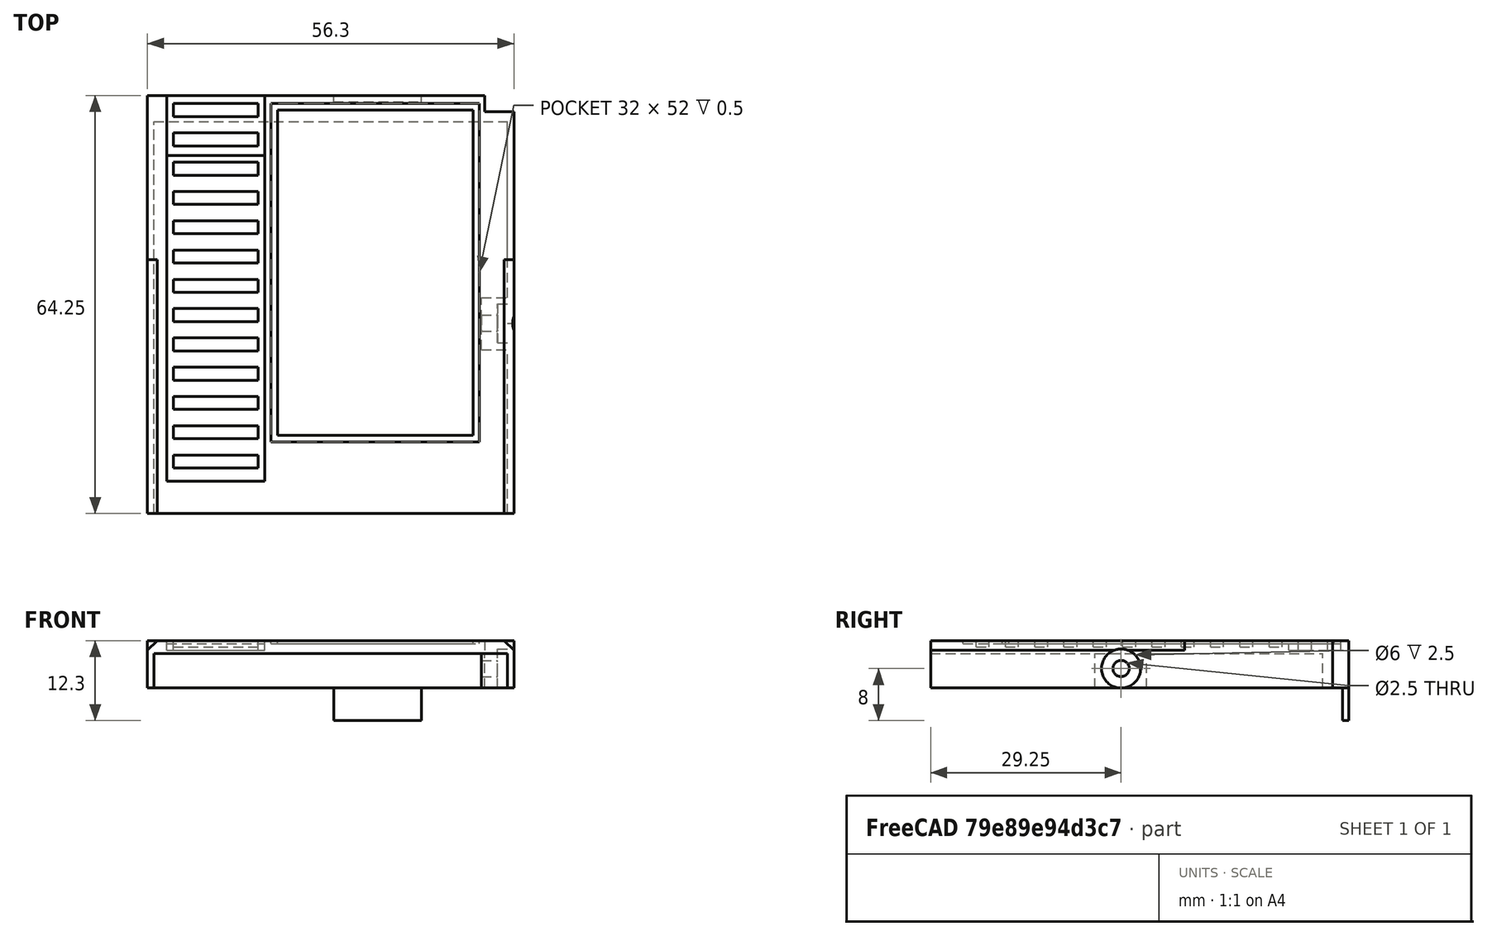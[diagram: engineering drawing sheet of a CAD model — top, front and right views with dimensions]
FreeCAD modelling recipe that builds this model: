
FCSTD DOCUMENT  (FreeCAD 0.18R16131 (Git))
Label: GBC_cart_cover
License: All rights reserved
LicenseURL: http://en.wikipedia.org/wiki/All_rights_reserved
objects: Part::Box×26, Part::Cut×7, Part::MultiFuse×5, Part::Cylinder×2, Part::Chamfer×1
note: 41 computed .brp shape members not serialized (recipe doc carries the construction recipe); baked Part::Feature solids carry a one-line shape summary decoded from their .brp

FEATURE [Part::Box] Box  label="Cube(outer_base)"
  AttacherType = Attacher::AttachEngine3D
  Height = 5.3
  Length = 56.3
  Width = 64.25
FEATURE [Part::Box] Box001  label="Cube(corner_inner)"
  AttacherType = Attacher::AttachEngine3D
  Height = 5.3
  Length = 4.5
  Placement = pos=(51.8,61.75,0) rot=(0,0,1;0rad)
  Width = 2.5
FEATURE [Part::Box] Box007  label="Cube(top_cover_top_half)"
  AttacherType = Attacher::AttachEngine3D
  Height = 2
  Length = 56.3
  Placement = pos=(0,39,5.3) rot=(0,0,1;0rad)
  Width = 25.25
FEATURE [Part::Box] Box008  label="Cube001(top_cover_bottom_half)"
  AttacherType = Attacher::AttachEngine3D
  Height = 2
  Length = 56.3
  Placement = pos=(0,0,5.3) rot=(0,0,1;0rad)
  Width = 39
FEATURE [Part::Box] Box010  label="Cube(top_corner_cut)"
  AttacherType = Attacher::AttachEngine3D
  Height = 10
  Length = 10
  Placement = pos=(51.8,61.75,0) rot=(0,0,1;0rad)
  Width = 10
FEATURE [Part::Cut] Cut006
  Base = -> Box007
  Tool = -> Box010
FEATURE [Part::Box] Box017  label="Cube(game_lable_inner)"
  AttacherType = Attacher::AttachEngine3D
  Height = 0.5
  Length = 30
  Placement = pos=(20,12,6.8) rot=(0,0,1;0rad)
  Width = 50
FEATURE [Part::Box] Box018  label="Cube(cube_strips)"
  AttacherType = Attacher::AttachEngine3D
  Height = 0.5
  Length = 15
  Placement = pos=(3,5,6.8) rot=(0,0,1;0rad)
  Width = 53
FEATURE [Part::Box] Box019  label="Cube(cube_strip_top)"
  AttacherType = Attacher::AttachEngine3D
  Height = 1.5
  Length = 15
  Placement = pos=(3,55,5.8) rot=(0,0,1;0rad)
  Width = 9.25
FEATURE [Part::Box] Box020  label="Cube(ladders)"
  AttacherType = Attacher::AttachEngine3D
  Height = 1
  Length = 13
  Placement = pos=(4,7,6.3) rot=(0,0,1;0rad)
  Width = 2
FEATURE [Part::Box] Box021  label="Cube(ladders)001"
  AttacherType = Attacher::AttachEngine3D
  Height = 1
  Length = 13
  Placement = pos=(4,11.5,6.3) rot=(0,0,1;0rad)
  Width = 2
FEATURE [Part::Box] Box022  label="Cube(ladders)002"
  AttacherType = Attacher::AttachEngine3D
  Height = 1
  Length = 13
  Placement = pos=(4,16,6.3) rot=(0,0,1;0rad)
  Width = 2
FEATURE [Part::Box] Box023  label="Cube(ladders)003"
  AttacherType = Attacher::AttachEngine3D
  Height = 1
  Length = 13
  Placement = pos=(4,20.5,6.3) rot=(0,0,1;0rad)
  Width = 2
FEATURE [Part::Box] Box024  label="Cube(ladders)004"
  AttacherType = Attacher::AttachEngine3D
  Height = 1
  Length = 13
  Placement = pos=(4,25,6.3) rot=(0,0,1;0rad)
  Width = 2
FEATURE [Part::Box] Box025  label="Cube(ladders)005"
  AttacherType = Attacher::AttachEngine3D
  Height = 1
  Length = 13
  Placement = pos=(4,29.5,6.3) rot=(0,0,1;0rad)
  Width = 2
FEATURE [Part::Box] Box029  label="Cube(cube_strip_top_outer)"
  AttacherType = Attacher::AttachEngine3D
  Height = 1.5
  Length = 17
  Placement = pos=(2,55,5.8) rot=(0,0,1;0rad)
  Width = 9.25
FEATURE [Part::MultiFuse] Fusion003
  Shapes = -> [Cut006,Box029]
FEATURE [Part::Cut] Cut008
  Base = -> Fusion003
  Tool = -> Box019
FEATURE [Part::Box] Box030  label="Cube(ladders)009"
  AttacherType = Attacher::AttachEngine3D
  Height = 1
  Length = 13
  Placement = pos=(4,34,6.3) rot=(0,0,1;0rad)
  Width = 2
FEATURE [Part::Box] Box031  label="Cube(ladders)010"
  AttacherType = Attacher::AttachEngine3D
  Height = 1
  Length = 13
  Placement = pos=(4,38.5,6.3) rot=(0,0,1;0rad)
  Width = 2
FEATURE [Part::Box] Box032  label="Cube(ladders)011"
  AttacherType = Attacher::AttachEngine3D
  Height = 1
  Length = 13
  Placement = pos=(4,43,6.3) rot=(0,0,1;0rad)
  Width = 2
FEATURE [Part::Box] Box034  label="Cube(ladders)013"
  AttacherType = Attacher::AttachEngine3D
  Height = 1
  Length = 13
  Placement = pos=(4,47.5,6.3) rot=(0,0,1;0rad)
  Width = 2
FEATURE [Part::Box] Box035  label="Cube(ladders)014"
  AttacherType = Attacher::AttachEngine3D
  Height = 1
  Length = 13
  Placement = pos=(4,52,6.3) rot=(0,0,1;0rad)
  Width = 2
FEATURE [Part::Box] Box038  label="Cube(ladders)017"
  AttacherType = Attacher::AttachEngine3D
  Height = 1.5
  Length = 13
  Placement = pos=(4,56.5,5.8) rot=(0,0,1;0rad)
  Width = 2
FEATURE [Part::Box] Box040  label="Cube(ladders)019"
  AttacherType = Attacher::AttachEngine3D
  Height = 1.5
  Length = 13
  Placement = pos=(4,61,5.8) rot=(0,0,1;0rad)
  Width = 2
FEATURE [Part::Box] Box041  label="Cube(game_lable_outer)"
  AttacherType = Attacher::AttachEngine3D
  Height = 0.5
  Length = 32
  Placement = pos=(19,11,6.8) rot=(0,0,1;0rad)
  Width = 52
FEATURE [Part::Chamfer] Chamfer
  Base = -> Box008
  Edges = 2 edges r=1.5: [Edge2,Edge6]
FEATURE [Part::MultiFuse] Fusion004
  Shapes = -> [Cut008,Chamfer]
FEATURE [Part::Cut] Cut012
  Base = -> Fusion004
  Tool = -> Box018
FEATURE [Part::Cut] Cut013
  Base = -> Cut012
  Tool = -> Box041
FEATURE [Part::Box] Box042  label="Cube(outer_base)001"
  AttacherType = Attacher::AttachEngine3D
  Height = 5.3
  Length = 54.3
  Placement = pos=(1,0,0) rot=(0,0,1;0rad)
  Width = 60.25
FEATURE [Part::Cut] Cut
  Base = -> Box
  Tool = -> Box001
FEATURE [Part::Cut] Cut014
  Base = -> Cut
  Tool = -> Box042
FEATURE [Part::Box] Box043  label="Cube(sd_card_cover)"
  AttacherType = Attacher::AttachEngine3D
  Height = 5
  Length = 13.5
  Placement = pos=(28.6,63.25,-5) rot=(0,0,1;0rad)
  Width = 1
FEATURE [Part::Cylinder] Cylinder  label="Cylinder(screw_head)"
  Angle = 360
  AttacherType = Attacher::AttachEngine3D
  Height = 2.5
  Placement = pos=(53.8,29.25,3) rot=(0,1,0;1.5708rad)
  Radius = 3
FEATURE [Part::Cylinder] Cylinder001  label="Cylinder(screw_head)001"
  Angle = 360
  AttacherType = Attacher::AttachEngine3D
  Height = 2.5
  Placement = pos=(51.3,29.25,3) rot=(0,1,0;1.5708rad)
  Radius = 1.25
FEATURE [Part::Box] Box044  label="Cube(screw_block)"
  AttacherType = Attacher::AttachEngine3D
  Height = 5.3
  Length = 4
  Placement = pos=(51.3,25.2,0) rot=(0,0,1;0rad)
  Width = 8
FEATURE [Part::MultiFuse] Fusion
  Shapes = -> [Cylinder,Cylinder001]
FEATURE [Part::MultiFuse] Fusion005
  Shapes = -> [Box044,Cut014]
FEATURE [Part::MultiFuse] Fusion006
  Shapes = -> [Fusion005,Cut013]
FEATURE [Part::Cut] Cut015
  Base = -> Fusion006
  Tool = -> Fusion
